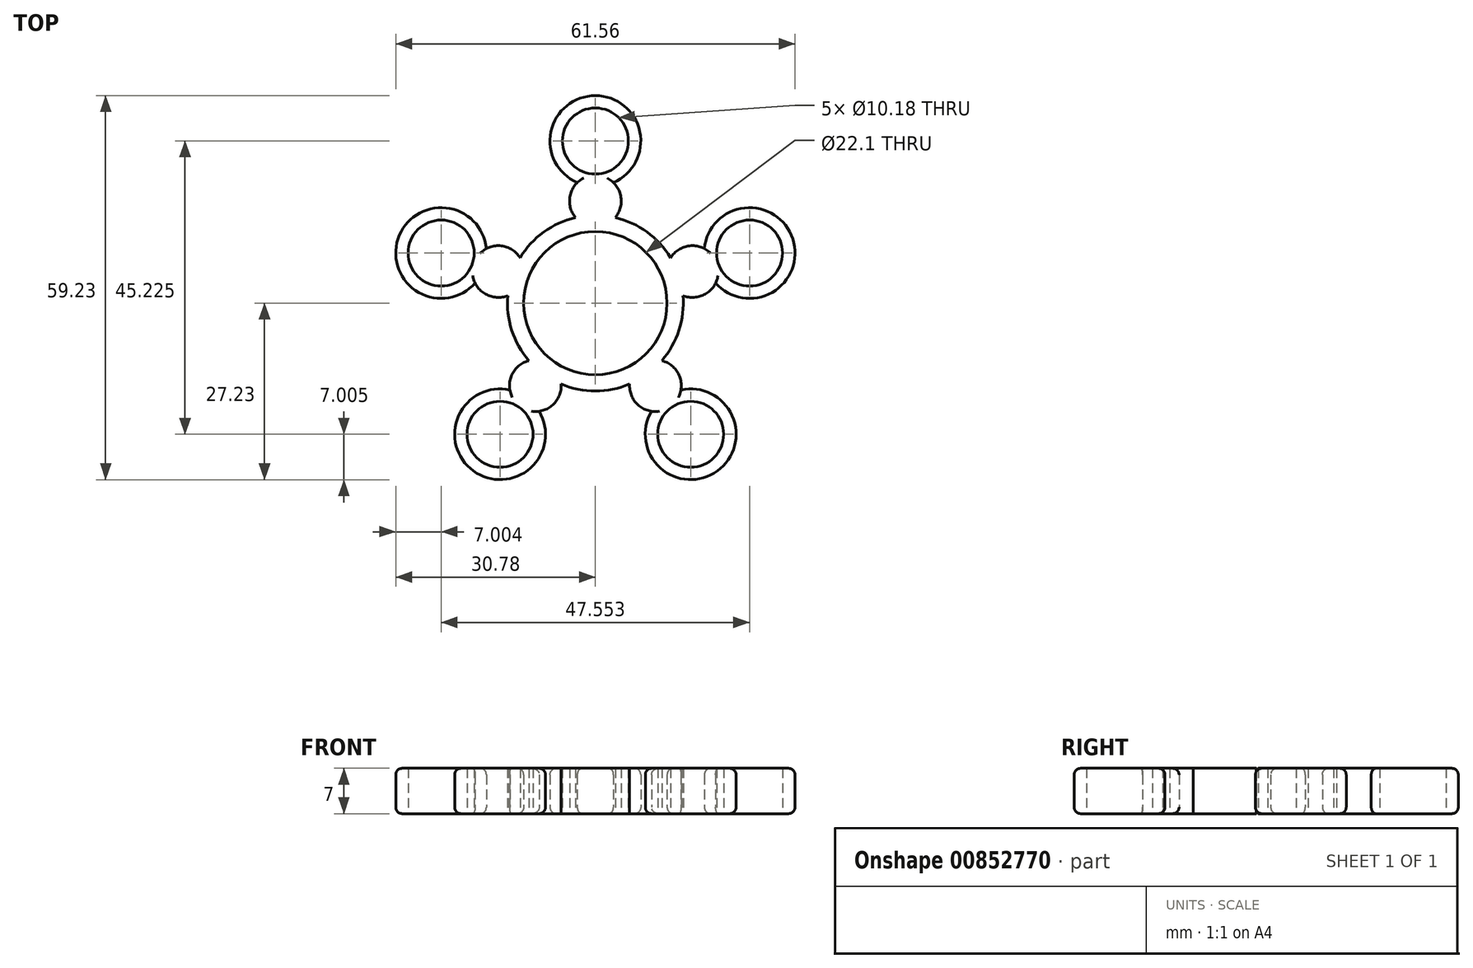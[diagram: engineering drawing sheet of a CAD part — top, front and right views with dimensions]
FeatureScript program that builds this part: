
annotation { "Feature Type Name" : "Feature", "Feature Type Description" : "" }
export const myFeature = defineFeature(function(context is Context, id is Id, definition is map)
    precondition{}
    {
        {
            var Q0;
            Q0=qCreatedBy(makeId("Top.planeOp"),FACE);
            var sketch = newSketch(context, id + "F0", { "sketchPlane" : qUnion([Q0])});
            skCircle(sketch, "E0", {"center": v(0, 0) * mm, "radius": 11.05 * mm});
            skArc(sketch, "E1", {"start": v(-3.07, 13.2) * mm, "mid": v(-7.96, 10.96) * mm, "end": v(-11.6, 7) * mm});
            skCircle(sketch, "E2", {"center": v(0, 25) * mm, "radius": 5.1 * mm});
            skArc(sketch, "E3", {"start": v(2.8, 18.58) * mm, "mid": v(0, 32) * mm, "end": v(-2.8, 18.58) * mm});
            skArc(sketch, "E4", {"start": v(-2.8, 18.58) * mm, "mid": v(-3.98, 15.94) * mm, "end": v(-3.07, 13.2) * mm});
            skCircle(sketch, "E5.1.0", {"center": v(-23.78, 7.73) * mm, "radius": 5.1 * mm});
            skArc(sketch, "E5.1.1", {"start": v(-16.8, 8.4) * mm, "mid": v(-30.43, 9.89) * mm, "end": v(-18.54, 3.08) * mm});
            skArc(sketch, "E5.1.2", {"start": v(-18.54, 3.08) * mm, "mid": v(-16.4, 1.14) * mm, "end": v(-13.5, 1.16) * mm});
            skCircle(sketch, "E5.2.0", {"center": v(-14.7, -20.23) * mm, "radius": 5.1 * mm});
            skArc(sketch, "E5.2.1", {"start": v(-13.19, -13.39) * mm, "mid": v(-18.8, -25.89) * mm, "end": v(-8.66, -16.68) * mm});
            skArc(sketch, "E5.2.2", {"start": v(-10.24, -8.87) * mm, "mid": v(-12.6, -10.56) * mm, "end": v(-13.19, -13.39) * mm});
            skCircle(sketch, "E5.3.0", {"center": v(14.7, -20.23) * mm, "radius": 5.1 * mm});
            skArc(sketch, "E5.3.1", {"start": v(8.66, -16.68) * mm, "mid": v(18.8, -25.89) * mm, "end": v(13.19, -13.39) * mm});
            skArc(sketch, "E5.3.2", {"start": v(5.27, -12.48) * mm, "mid": v(6.15, -15.24) * mm, "end": v(8.66, -16.68) * mm});
            skCircle(sketch, "E5.4.0", {"center": v(23.78, 7.73) * mm, "radius": 5.1 * mm});
            skArc(sketch, "E5.4.1", {"start": v(18.54, 3.08) * mm, "mid": v(30.43, 9.89) * mm, "end": v(16.8, 8.4) * mm});
            skArc(sketch, "E5.4.2", {"start": v(16.8, 8.4) * mm, "mid": v(13.93, 8.71) * mm, "end": v(11.6, 7) * mm});
            skArc(sketch, "E6.trimOffspring", {"start": v(3.07, 13.2) * mm, "mid": v(3.98, 15.94) * mm, "end": v(2.8, 18.58) * mm});
            skArc(sketch, "E7.trimOffspring", {"start": v(11.6, 7) * mm, "mid": v(7.96, 10.96) * mm, "end": v(3.07, 13.2) * mm});
            skArc(sketch, "E8.trimOffspring", {"start": v(13.5, 1.16) * mm, "mid": v(16.4, 1.14) * mm, "end": v(18.54, 3.08) * mm});
            skArc(sketch, "E9.trimOffspring", {"start": v(-11.6, 7) * mm, "mid": v(-13.93, 8.71) * mm, "end": v(-16.8, 8.4) * mm});
            skArc(sketch, "E10.trimOffspring", {"start": v(-13.5, 1.16) * mm, "mid": v(-12.89, -4.19) * mm, "end": v(-10.24, -8.87) * mm});
            skArc(sketch, "E11.trimOffspring", {"start": v(-8.66, -16.68) * mm, "mid": v(-6.15, -15.24) * mm, "end": v(-5.27, -12.48) * mm});
            skArc(sketch, "E12.trimOffspring", {"start": v(-5.27, -12.48) * mm, "mid": v(0, -13.55) * mm, "end": v(5.27, -12.48) * mm});
            skArc(sketch, "E13.trimOffspring", {"start": v(13.19, -13.39) * mm, "mid": v(12.6, -10.56) * mm, "end": v(10.24, -8.87) * mm});
            skArc(sketch, "E14.trimOffspring", {"start": v(10.24, -8.87) * mm, "mid": v(12.89, -4.19) * mm, "end": v(13.5, 1.16) * mm});
            skSolve(sketch);
        }
        {
            var Q0;
            Q0=makeQuery(id+"F0.imprint","IMPRINT",FACE,{"disambiguationData":[TD([[makeQuery(id+"F0.imprint","IMPRINT",EDGE,{"derivedFrom":sQuery(id+"F0.wireOp",EDGE,"E0")}),-1.0]])]});
            extrude(context, id + "F1", {"entities" : qUnion([Q0]), "depth" : 7 * mm, "offsetDistance" : 25 * mm});
        }
        {
            var Q0;
            Q0=makeQuery(id+"F1.opExtrude","CAP_EDGE",EDGE,{"disambiguationData":[OSD([sQuery(id+"F0.wireOp",EDGE,"E5.1.1")])],"isStart":false});
            var Q1;
            Q1=makeQuery(id+"F1.opExtrude","CAP_EDGE",EDGE,{"disambiguationData":[OSD([sQuery(id+"F0.wireOp",EDGE,"E5.2.1")])],"isStart":false});
            var Q2;
            Q2=makeQuery(id+"F1.opExtrude","CAP_EDGE",EDGE,{"disambiguationData":[OSD([sQuery(id+"F0.wireOp",EDGE,"E5.3.1")])],"isStart":false});
            var Q3;
            Q3=makeQuery(id+"F1.opExtrude","CAP_EDGE",EDGE,{"disambiguationData":[OSD([sQuery(id+"F0.wireOp",EDGE,"E5.4.1")])],"isStart":false});
            var Q4;
            Q4=makeQuery(id+"F1.opExtrude","CAP_EDGE",EDGE,{"disambiguationData":[OSD([sQuery(id+"F0.wireOp",EDGE,"E3")])],"isStart":false});
            var Q5;
            Q5=makeQuery(id+"F1.opExtrude","CAP_EDGE",EDGE,{"disambiguationData":[OSD([sQuery(id+"F0.wireOp",EDGE,"E5.4.1")])],"isStart":true});
            var Q6;
            Q6=makeQuery(id+"F1.opExtrude","CAP_EDGE",EDGE,{"disambiguationData":[OSD([sQuery(id+"F0.wireOp",EDGE,"E3")])],"isStart":true});
            var Q7;
            Q7=makeQuery(id+"F1.opExtrude","CAP_EDGE",EDGE,{"disambiguationData":[OSD([sQuery(id+"F0.wireOp",EDGE,"E5.1.1")])],"isStart":true});
            var Q8;
            Q8=makeQuery(id+"F1.opExtrude","CAP_EDGE",EDGE,{"disambiguationData":[OSD([sQuery(id+"F0.wireOp",EDGE,"E5.3.1")])],"isStart":true});
            var Q9;
            Q9=makeQuery(id+"F1.opExtrude","CAP_EDGE",EDGE,{"disambiguationData":[OSD([sQuery(id+"F0.wireOp",EDGE,"E5.2.1")])],"isStart":true});
            fillet(context, id + "F2", {"entities" : qUnion([Q0, Q1, Q2, Q3, Q4, Q5, Q6, Q7, Q8, Q9]), "radius" : 1 * mm, "tangentPropagation" : true, "allowEdgeOverflow" : false});
        }
        {
            var Q0;
            Q0=makeQuery(id+"F1.opExtrude","CAP_EDGE",EDGE,{"disambiguationData":[OSD([sQuery(id+"F0.wireOp",EDGE,"E0")])],"isStart":true});
            var Q1;
            Q1=makeQuery(id+"F1.opExtrude","CAP_EDGE",EDGE,{"disambiguationData":[OSD([sQuery(id+"F0.wireOp",EDGE,"E0")])],"isStart":false});
            fillet(context, id + "F3", {"entities" : qUnion([Q0, Q1]), "radius" : 1 * mm, "tangentPropagation" : true, "allowEdgeOverflow" : false});
        }
    });
